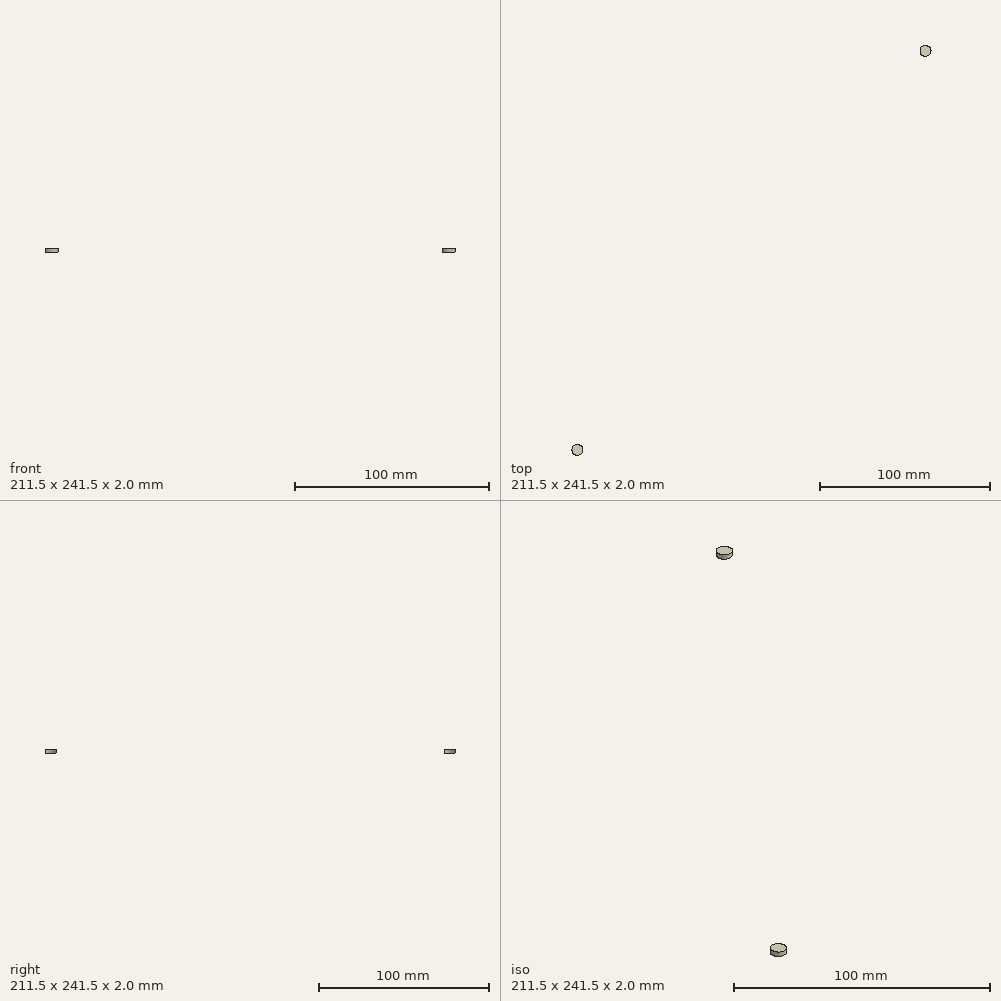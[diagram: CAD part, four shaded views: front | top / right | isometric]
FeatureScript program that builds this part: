
annotation { "Feature Type Name" : "Feature", "Feature Type Description" : "" }
export const myFeature = defineFeature(function(context is Context, id is Id, definition is map)
    precondition{}
    {
        {
            var Q0;
            Q0=qCreatedBy(makeId("Top.planeOp"),FACE);
            var sketch = newSketch(context, id + "F0", { "sketchPlane" : qUnion([Q0])});
            skLineSegment(sketch, "E0.bottom", {"start": v(112.5, -127.5) * mm, "end": v(-112.5, -127.5) * mm});
            skLineSegment(sketch, "E0.top", {"start": v(112.5, 127.5) * mm, "end": v(-112.5, 127.5) * mm});
            skLineSegment(sketch, "E0.left", {"start": v(112.5, -127.5) * mm, "end": v(112.5, 127.5) * mm});
            skLineSegment(sketch, "E0.right", {"start": v(-112.5, -127.5) * mm, "end": v(-112.5, 127.5) * mm});
            skPoint(sketch, "E0.middle", {"position": v(0, 0) * mm});
            skSolve(sketch);
        }
        {
            var Q0;
            Q0=makeQuery(id+"F0.imprint","IMPRINT",FACE,{"disambiguationData":[TD([[makeQuery(id+"F0.imprint","IMPRINT",EDGE,{"derivedFrom":sQuery(id+"F0.wireOp",EDGE,"E0.bottom")}),-1.0]])]});
            extrude(context, id + "F1", {"entities" : qUnion([Q0]), "depth" : 2 * mm});
        }
        {
            var Q0;
            Q0=makeQuery(id+"F1.opExtrude","CAP_FACE",FACE,{"disambiguationData":[OSD([sQuery(id+"F0.wireOp",EDGE,"E0.bottom"),sQuery(id+"F0.wireOp",EDGE,"E0.top"),sQuery(id+"F0.wireOp",EDGE,"E0.left"),sQuery(id+"F0.wireOp",EDGE,"E0.right")])],"isStart":false});
            var sketch = newSketch(context, id + "F2", { "sketchPlane" : qUnion([Q0])});
            skCircle(sketch, "E1", {"center": v(-102.5, 117.5) * mm, "radius": 3.25 * mm});
            skCircle(sketch, "E2.MirrorC", {"center": v(102.5, 117.5) * mm, "radius": 3.25 * mm});
            skCircle(sketch, "E3.MirrorC", {"center": v(-102.5, -117.5) * mm, "radius": 3.25 * mm});
            skCircle(sketch, "E4.MirrorC", {"center": v(102.5, -117.5) * mm, "radius": 3.25 * mm});
            skSolve(sketch);
        }
        {
            var Q0;
            Q0=makeQuery(id+"F2.imprint","IMPRINT",FACE,{"disambiguationData":[TD([[makeQuery(id+"F2.imprint","IMPRINT",EDGE,{"derivedFrom":sQuery(id+"F2.wireOp",EDGE,"E1")}),1.0]])]});
            var Q1;
            Q1=makeQuery(id+"F2.imprint","IMPRINT",FACE,{"disambiguationData":[TD([[makeQuery(id+"F2.imprint","IMPRINT",EDGE,{"derivedFrom":sQuery(id+"F2.wireOp",EDGE,"E2.MirrorC")}),-1.0]])]});
            var Q2;
            Q2=makeQuery(id+"F2.imprint","IMPRINT",FACE,{"disambiguationData":[TD([[makeQuery(id+"F2.imprint","IMPRINT",EDGE,{"derivedFrom":sQuery(id+"F2.wireOp",EDGE,"E3.MirrorC")}),-1.0]])]});
            var Q3;
            Q3=makeQuery(id+"F2.imprint","IMPRINT",FACE,{"disambiguationData":[TD([[makeQuery(id+"F2.imprint","IMPRINT",EDGE,{"derivedFrom":sQuery(id+"F2.wireOp",EDGE,"E4.MirrorC")}),1.0]])]});
            extrude(context, id + "F3", {"entities" : qUnion([Q0, Q1, Q2, Q3]), "operationType" : NewBodyOperationType.REMOVE, "oppositeDirection" : true, "depth" : 25 * mm});
        }
    });
